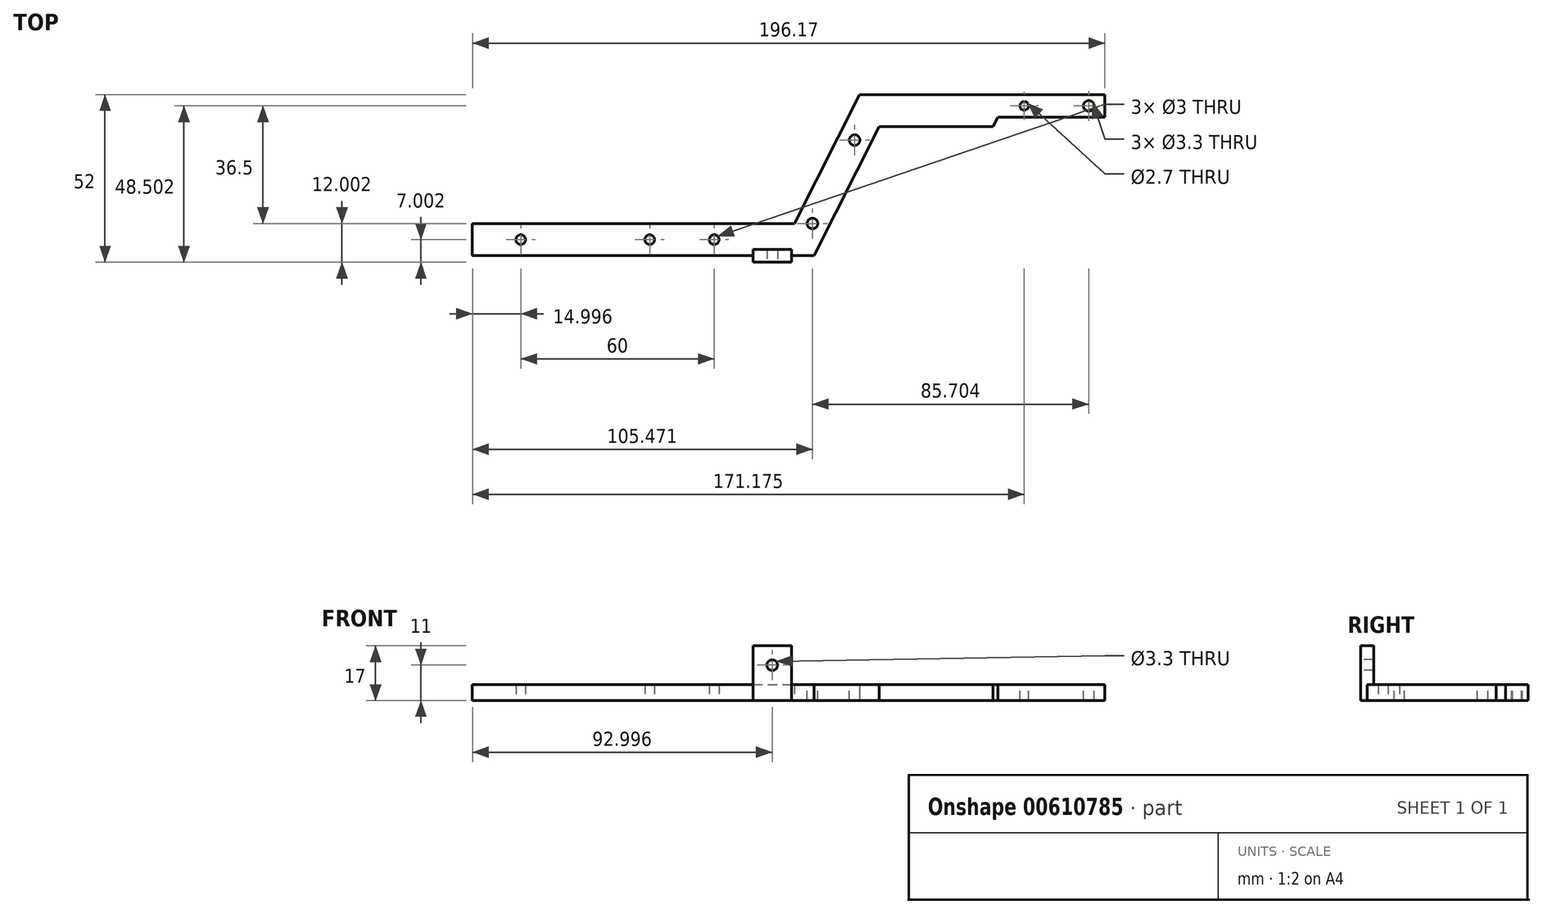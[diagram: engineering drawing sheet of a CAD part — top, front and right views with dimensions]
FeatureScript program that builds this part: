
annotation { "Feature Type Name" : "Feature", "Feature Type Description" : "" }
export const myFeature = defineFeature(function(context is Context, id is Id, definition is map)
    precondition{}
    {
        {
            var Q0;
            Q0=qCreatedBy(makeId("Top.planeOp"),FACE);
            var sketch = newSketch(context, id + "F0", { "sketchPlane" : qUnion([Q0])});
            skLineSegment(sketch, "E0", {"start": v(-151.91, -45.93) * mm, "end": v(-52.04, -45.93) * mm});
            skLineSegment(sketch, "E1.0", {"start": v(-151.91, -55.93) * mm, "end": v(-45.89, -55.93) * mm});
            skLineSegment(sketch, "E2.0", {"start": v(-31.91, -5.93) * mm, "end": v(-31.84, -5.93) * mm});
            skLineSegment(sketch, "E3", {"start": v(-31.91, -5.93) * mm, "end": v(-31.91, -6.08) * mm});
            skPoint(sketch, "E3.endSnap0", {"position": v(-31.91, -20.93) * mm});
            skLineSegment(sketch, "E4", {"start": v(-151.91, -45.93) * mm, "end": v(-151.91, -55.93) * mm});
            skPoint(sketch, "E5.orphan", {"position": v(-31.91, -83.57) * mm});
            skPoint(sketch, "E6.orphan", {"position": v(-31.91, 4.07) * mm});
            skLineSegment(sketch, "E7", {"start": v(-52.04, -45.93) * mm, "end": v(-31.84, -5.93) * mm});
            skPoint(sketch, "E8.orphan", {"position": v(-41.91, 4.07) * mm});
            skLineSegment(sketch, "E9.trimOffspring", {"start": v(-31.91, -6.08) * mm, "end": v(-31.91, -5.93) * mm});
            skPoint(sketch, "E10.orphan", {"position": v(-41.91, -45.93) * mm});
            skLineSegment(sketch, "E11", {"start": v(-25.68, -15.93) * mm, "end": v(-45.89, -55.93) * mm});
            skPoint(sketch, "E12.0.start.orphan", {"position": v(-31.91, -45.93) * mm});
            skPoint(sketch, "E13.orphan", {"position": v(-35.66, 0) * mm});
            skPoint(sketch, "E14.orphan", {"position": v(38.09, 4.07) * mm});
            skCircle(sketch, "E15", {"center": v(-76.91, -50.93) * mm, "radius": 1.5 * mm});
            skCircle(sketch, "E16", {"center": v(-96.91, -50.93) * mm, "radius": 1.5 * mm});
            skCircle(sketch, "E17", {"center": v(-136.91, -50.93) * mm, "radius": 1.5 * mm});
            skLineSegment(sketch, "E18", {"start": v(-31.91, -5.93) * mm, "end": v(27.96, -5.93) * mm});
            skLineSegment(sketch, "E19.0", {"start": v(-25.68, -15.93) * mm, "end": v(9.57, -15.93) * mm});
            skPoint(sketch, "E20.orphan", {"position": v(-40.25, -5.93) * mm});
            skLineSegment(sketch, "E21", {"start": v(44.26, -5.93) * mm, "end": v(27.96, -5.93) * mm});
            skLineSegment(sketch, "E22", {"start": v(44.26, -5.93) * mm, "end": v(44.26, -12.93) * mm});
            skPoint(sketch, "E23.orphan", {"position": v(44.26, 0) * mm});
            skPoint(sketch, "E24.orphan", {"position": v(52.97, -5.93) * mm});
            skLineSegment(sketch, "E25", {"start": v(11.09, -12.93) * mm, "end": v(44.26, -12.93) * mm});
            skLineSegment(sketch, "E26", {"start": v(11.09, -12.93) * mm, "end": v(9.57, -15.93) * mm});
            skPoint(sketch, "E27.start.orphan", {"position": v(11.09, -15.93) * mm});
            skSolve(sketch);
        }
        {
            var Q0;
            {var subQ1=sQuery(id+"F0.wireOp",EDGE,"E0");Q0=makeQuery(id+"F0.imprint","IMPRINT",FACE,{"disambiguationData":[TD([[makeQuery(id+"F0.imprint","IMPRINT",EDGE,{"derivedFrom":subQ1}),-1.0]])]});}
            extrude(context, id + "F1", {"entities" : qUnion([Q0]), "depth" : 5 * mm});
        }
        {
            var Q0;
            Q0=makeQuery(id+"F0.imprint","IMPRINT",FACE,{"disambiguationData":[TD([[makeQuery(id+"F0.imprint","IMPRINT",EDGE,{"derivedFrom":sQuery(id+"F0.wireOp",EDGE,"E15")}),1.0]])]});
            var Q1;
            Q1=makeQuery(id+"F0.imprint","IMPRINT",FACE,{"disambiguationData":[TD([[makeQuery(id+"F0.imprint","IMPRINT",EDGE,{"derivedFrom":sQuery(id+"F0.wireOp",EDGE,"E16")}),1.0]])]});
            extrude(context, id + "F2", {"entities" : qUnion([Q0, Q1]), "operationType" : NewBodyOperationType.REMOVE, "endBound" : BoundingType.THROUGH_ALL, "oppositeDirection" : true, "depth" : 25 * mm});
        }
        {
            var Q0;
            Q0=makeQuery(id+"F1.opExtrude","CAP_FACE",FACE,{"disambiguationData":[OSD([sQuery(id+"F0.wireOp",EDGE,"E0"),sQuery(id+"F0.wireOp",EDGE,"E1.0"),sQuery(id+"F0.wireOp",EDGE,"E4"),sQuery(id+"F0.wireOp",EDGE,"E7"),sQuery(id+"F0.wireOp",EDGE,"E11"),sQuery(id+"F0.wireOp",EDGE,"E15"),sQuery(id+"F0.wireOp",EDGE,"E16"),sQuery(id+"F0.wireOp",EDGE,"E17"),sQuery(id+"F0.wireOp",EDGE,"E18"),sQuery(id+"F0.wireOp",EDGE,"E19.0"),sQuery(id+"F0.wireOp",EDGE,"E21"),sQuery(id+"F0.wireOp",EDGE,"E22"),sQuery(id+"F0.wireOp",EDGE,"E25"),sQuery(id+"F0.wireOp",EDGE,"E26")])],"isStart":false});
            var sketch = newSketch(context, id + "F3", { "sketchPlane" : qUnion([Q0])});
            skCircle(sketch, "E28", {"center": v(-46.44, -45.93) * mm, "radius": 1.65 * mm});
            skCircle(sketch, "E29", {"center": v(-33.36, -20.04) * mm, "radius": 1.65 * mm});
            skCircle(sketch, "E30", {"center": v(19.26, -9.43) * mm, "radius": 1.35 * mm});
            skCircle(sketch, "E31", {"center": v(39.26, -9.43) * mm, "radius": 1.65 * mm});
            skSolve(sketch);
        }
        {
            var Q0;
            Q0=makeQuery(id+"F3.imprint","IMPRINT",FACE,{"disambiguationData":[TD([[makeQuery(id+"F3.imprint","IMPRINT",EDGE,{"derivedFrom":sQuery(id+"F3.wireOp",EDGE,"E31")}),1.0]])]});
            var Q1;
            Q1=makeQuery(id+"F3.imprint","IMPRINT",FACE,{"disambiguationData":[TD([[makeQuery(id+"F3.imprint","IMPRINT",EDGE,{"derivedFrom":sQuery(id+"F3.wireOp",EDGE,"E30")}),1.0]])]});
            var Q2;
            Q2=makeQuery(id+"F3.imprint","IMPRINT",FACE,{"disambiguationData":[TD([[makeQuery(id+"F3.imprint","IMPRINT",EDGE,{"derivedFrom":sQuery(id+"F3.wireOp",EDGE,"E29")}),1.0]])]});
            var Q3;
            Q3=makeQuery(id+"F3.imprint","IMPRINT",FACE,{"disambiguationData":[TD([[makeQuery(id+"F3.imprint","IMPRINT",EDGE,{"derivedFrom":sQuery(id+"F3.wireOp",EDGE,"E28")}),1.0]])]});
            extrude(context, id + "F4", {"entities" : qUnion([Q0, Q1, Q2, Q3]), "operationType" : NewBodyOperationType.REMOVE, "endBound" : BoundingType.THROUGH_ALL, "oppositeDirection" : true, "depth" : 25 * mm, "offsetDistance" : 25 * mm});
        }
        {
            var Q0;
            Q0=makeQuery(id+"F1.opExtrude","CAP_FACE",FACE,{"disambiguationData":[OSD([sQuery(id+"F0.wireOp",EDGE,"E0"),sQuery(id+"F0.wireOp",EDGE,"E1.0"),sQuery(id+"F0.wireOp",EDGE,"E4"),sQuery(id+"F0.wireOp",EDGE,"E7"),sQuery(id+"F0.wireOp",EDGE,"E11"),sQuery(id+"F0.wireOp",EDGE,"E15"),sQuery(id+"F0.wireOp",EDGE,"E16"),sQuery(id+"F0.wireOp",EDGE,"E17"),sQuery(id+"F0.wireOp",EDGE,"E18"),sQuery(id+"F0.wireOp",EDGE,"E19.0"),sQuery(id+"F0.wireOp",EDGE,"E21"),sQuery(id+"F0.wireOp",EDGE,"E22"),sQuery(id+"F0.wireOp",EDGE,"E25"),sQuery(id+"F0.wireOp",EDGE,"E26")])],"isStart":false});
            var sketch = newSketch(context, id + "F5", { "sketchPlane" : qUnion([Q0])});
            skLineSegment(sketch, "E32.bottom", {"start": v(-64.91, -53.93) * mm, "end": v(-52.91, -53.93) * mm});
            skLineSegment(sketch, "E32.top", {"start": v(-64.91, -57.93) * mm, "end": v(-52.91, -57.93) * mm});
            skLineSegment(sketch, "E32.left", {"start": v(-64.91, -53.93) * mm, "end": v(-64.91, -57.93) * mm});
            skLineSegment(sketch, "E32.right", {"start": v(-52.91, -53.93) * mm, "end": v(-52.91, -57.93) * mm});
            skSolve(sketch);
        }
        {
            var Q0;
            {var subQ0=sQuery(id+"F5.wireOp",EDGE,"E32.bottom");Q0=makeQuery(id+"F5.imprint","IMPRINT",FACE,{"disambiguationData":[TD([[makeQuery(id+"F5.imprint","IMPRINT",EDGE,{"derivedFrom":subQ0}),-1.0]])]});}
            var Q1;
            {var subQ0=sQuery(id+"F5.wireOp",EDGE,"E32.top");Q1=makeQuery(id+"F5.imprint","IMPRINT",FACE,{"disambiguationData":[TD([[makeQuery(id+"F5.imprint","IMPRINT",EDGE,{"derivedFrom":subQ0}),1.0]])]});}
            extrude(context, id + "F6", {"entities" : qUnion([Q0, Q1]), "operationType" : NewBodyOperationType.ADD, "depth" : 12 * mm, "offsetDistance" : 25 * mm});
        }
        {
            var Q0;
            Q0=makeQuery(id+"F6.opExtrude","CAP_FACE",FACE,{"disambiguationData":[OSD([sQuery(id+"F5.wireOp",EDGE,"E32.bottom"),sQuery(id+"F5.wireOp",EDGE,"E32.top"),sQuery(id+"F5.wireOp",EDGE,"E32.left"),sQuery(id+"F5.wireOp",EDGE,"E32.right")])],"isStart":true});
            extrude(context, id + "F7", {"entities" : qUnion([Q0]), "operationType" : NewBodyOperationType.ADD, "depth" : 5 * mm, "offsetDistance" : 25 * mm});
        }
        {
            var Q0;
            {var subQ0=sQuery(id+"F5.wireOp",EDGE,"E32.top");Q0=makeQuery(id+"F7.boolean.opBoolean","MERGE",FACE,{"derivedFrom":[makeQuery(id+"F6.opExtrude","SWEPT_FACE",FACE,{"disambiguationData":[OSD([subQ0])]}),makeQuery(id+"F7.opExtrude","SWEPT_FACE",FACE,{"disambiguationData":[OSD([subQ0])]})]});}
            var sketch = newSketch(context, id + "F8", { "sketchPlane" : qUnion([Q0])});
            skCircle(sketch, "E33", {"center": v(-58.91, 11) * mm, "radius": 1.65 * mm});
            skSolve(sketch);
        }
        {
            var Q0;
            Q0=makeQuery(id+"F8.imprint","IMPRINT",FACE,{"disambiguationData":[TD([[makeQuery(id+"F8.imprint","IMPRINT",EDGE,{"derivedFrom":sQuery(id+"F8.wireOp",EDGE,"E33")}),1.0]])]});
            extrude(context, id + "F9", {"entities" : qUnion([Q0]), "operationType" : NewBodyOperationType.REMOVE, "endBound" : BoundingType.THROUGH_ALL, "oppositeDirection" : true, "depth" : 25 * mm, "offsetDistance" : 25 * mm});
        }
    });
